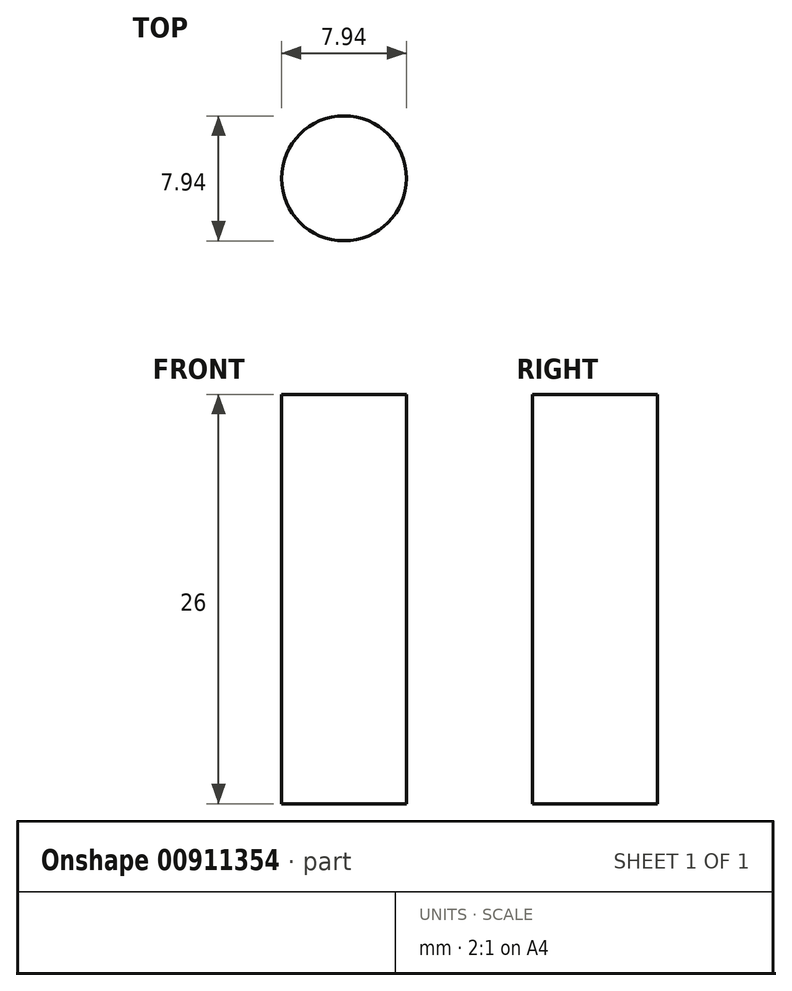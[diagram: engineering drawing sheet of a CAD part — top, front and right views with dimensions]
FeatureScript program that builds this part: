
annotation { "Feature Type Name" : "Feature", "Feature Type Description" : "" }
export const myFeature = defineFeature(function(context is Context, id is Id, definition is map)
    precondition{}
    {
        {
            var Q0;
            Q0=qCreatedBy(makeId("Top.planeOp"),FACE);
            var sketch = newSketch(context, id + "F0", { "sketchPlane" : qUnion([Q0])});
            skCircle(sketch, "E0", {"center": v(0, 0) * mm, "radius": 3.97 * mm});
            skSolve(sketch);
        }
        {
            var Q0;
            Q0=makeQuery(id+"F0.imprint","IMPRINT",FACE,{"disambiguationData":[TD([[makeQuery(id+"F0.imprint","IMPRINT",EDGE,{"derivedFrom":sQuery(id+"F0.wireOp",EDGE,"E0")}),1.0]])]});
            var Q1;
            Q1=sQuery(id+"F0.wireOp",EDGE,"E0");
            extrude(context, id + "F1", {"entities" : qUnion([Q0]), "surfaceEntities" : qUnion([Q1]), "endBound" : BoundingType.SYMMETRIC, "depth" : 26 * mm, "offsetDistance" : 25 * mm});
        }
    });
